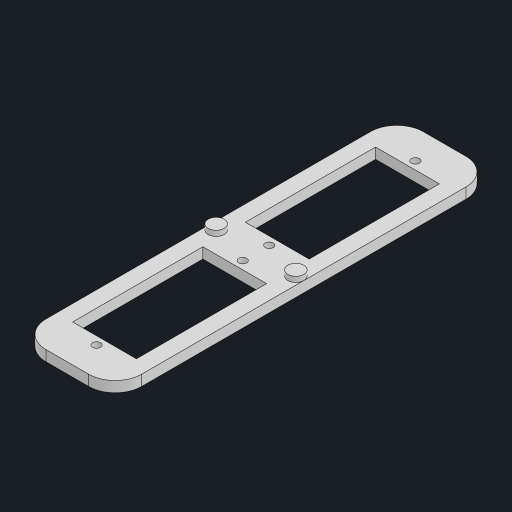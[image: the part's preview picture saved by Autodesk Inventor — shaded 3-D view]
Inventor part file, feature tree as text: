
AUTODESK INVENTOR PART (.ipt)
format: ipt  version: 2023 (Build 270158000, 158)  size: 145,408 bytes
history: native  units: mm
features: other x2, sketch x2, extrude x2, hole x1, mirror x1, fillet x1
ambient origin geometry x8: Origin, YZ Plane, XZ Plane, XY Plane, X Axis, Y Axis, Z Axis, Center Point
bodies: Body1 (feature_tree)
feature tree (9):
  other  "ソリッド1"
  sketch  "スケッチ1"
  extrude  "押し出し1"  Depth=24.5mm
  hole  "穴1"  [1 undecoded]
  mirror  "ミラー1"
  fillet  "フィレット1"  Radius=3.0mm
  other  "位置合わせ"
  extrude  "押し出し2"  Depth=4.0mm
  sketch  "スケッチ2"
note: 1 required parameter value undecoded (feature->parameter linkage not recoverable at this tier; creation-order binding heuristic only, values carry confidence <= 0.55)
